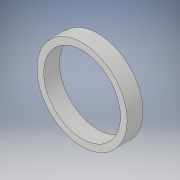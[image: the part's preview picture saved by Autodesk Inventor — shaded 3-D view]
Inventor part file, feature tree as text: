
AUTODESK INVENTOR PART (.ipt)
format: ipt  version: 2019 (Build 230136000, 136)  size: 104,448 bytes
history: native  units: mm
features: extrude x2, sketch x2
ambient origin geometry x8: Origin, YZ Plane, XZ Plane, XY Plane, X Axis, Y Axis, Z Axis, Center Point
bodies: Solid1 (feature_tree)
feature tree (4):
  extrude  "Extrusion1"  Depth=6.0mm TaperAngle=0.0deg
  extrude  "Extrusion2"  Depth=6.0mm TaperAngle=0.0deg
  sketch  "Sketch1"  dims[d0=34.0mm d1=6.0mm d2=0.0mm]
  sketch  "Sketch2"  dims[d3=29.0mm d4=6.0mm d5=0.0mm]
